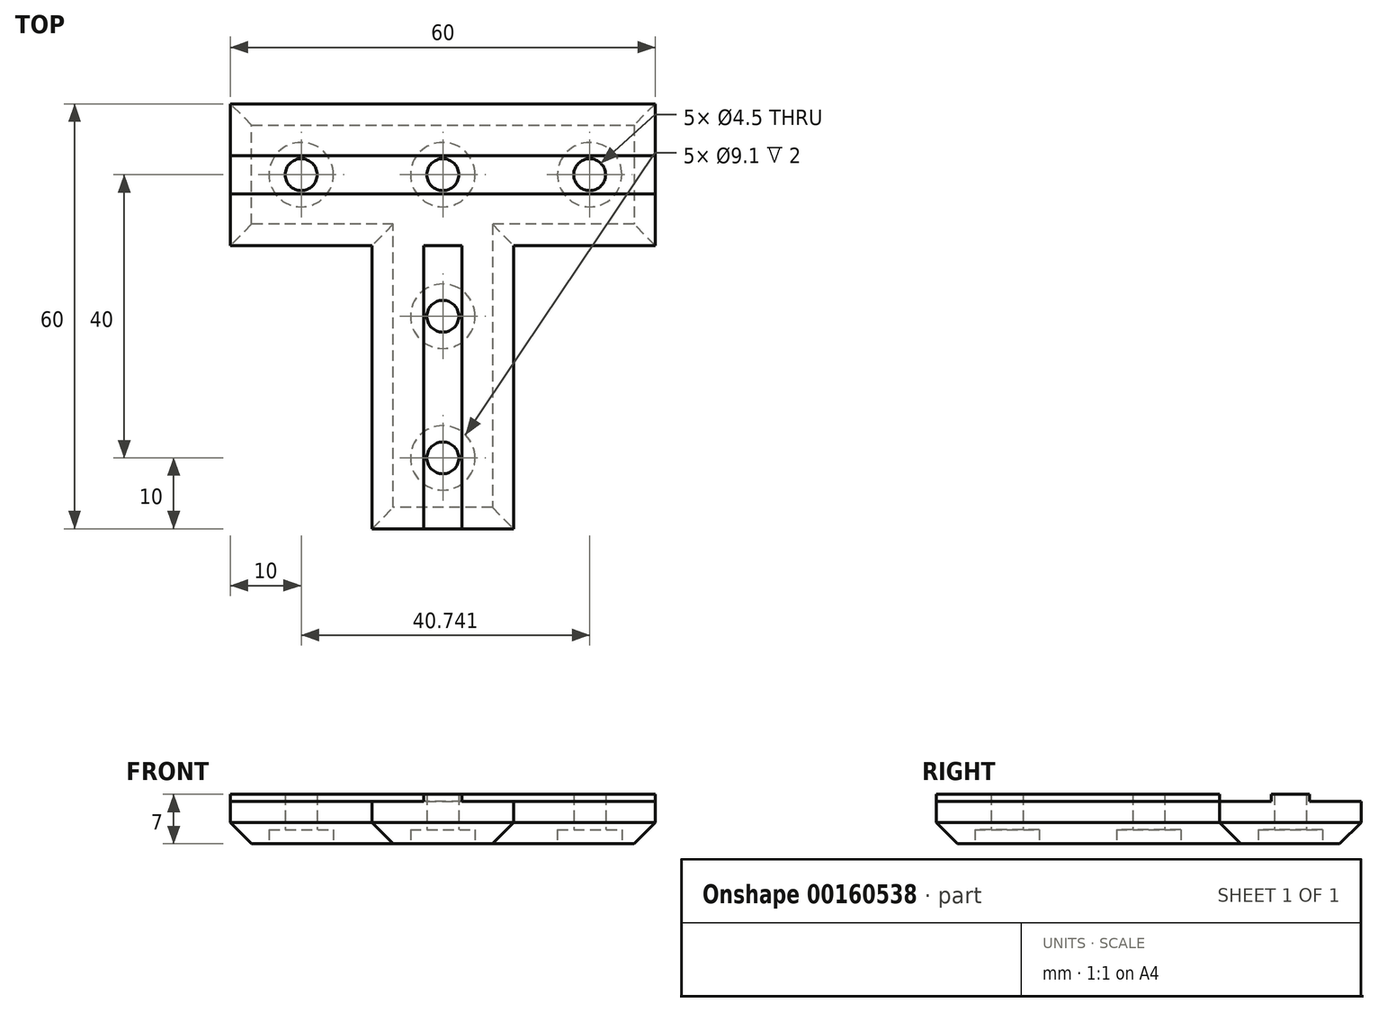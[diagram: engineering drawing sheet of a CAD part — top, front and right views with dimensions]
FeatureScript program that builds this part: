
annotation { "Feature Type Name" : "Feature", "Feature Type Description" : "" }
export const myFeature = defineFeature(function(context is Context, id is Id, definition is map)
    precondition{}
    {
        {
            var Q0;
            Q0=qCreatedBy(makeId("Top.planeOp"),FACE);
            var sketch = newSketch(context, id + "F0", { "sketchPlane" : qUnion([Q0])});
            skLineSegment(sketch, "E0", {"start": v(0, 0) * mm, "end": v(0, 20) * mm, "construction": true});
            skLineSegment(sketch, "E1", {"start": v(0, 0) * mm, "end": v(0, -40) * mm, "construction": true});
            skLineSegment(sketch, "E2", {"start": v(-10, 0) * mm, "end": v(-30, 0) * mm});
            skLineSegment(sketch, "E3", {"start": v(0, 20) * mm, "end": v(-30, 20) * mm});
            skLineSegment(sketch, "E4", {"start": v(-30, 20) * mm, "end": v(-30, 0) * mm});
            skLineSegment(sketch, "E5", {"start": v(0, 20) * mm, "end": v(30, 20) * mm});
            skLineSegment(sketch, "E6", {"start": v(30, 20) * mm, "end": v(30, 0) * mm});
            skLineSegment(sketch, "E7", {"start": v(30, 0) * mm, "end": v(10, 0) * mm});
            skLineSegment(sketch, "E8", {"start": v(0, -40) * mm, "end": v(10, -40) * mm});
            skLineSegment(sketch, "E9", {"start": v(10, -40) * mm, "end": v(10, 0) * mm});
            skLineSegment(sketch, "E10", {"start": v(0, -40) * mm, "end": v(-10, -40) * mm});
            skLineSegment(sketch, "E11", {"start": v(-10, -40) * mm, "end": v(-10, 0) * mm});
            skSolve(sketch);
        }
        {
            var Q0;
            Q0=qSketchRegion(id+"F0",true);
            extrude(context, id + "F1", {"entities" : qUnion([Q0]), "depth" : 6 * mm});
        }
        {
            var Q0;
            Q0=makeQuery(id+"F1.opExtrude","CAP_FACE",FACE,{"disambiguationData":[OSD([sQuery(id+"F0.wireOp",EDGE,"E2"),sQuery(id+"F0.wireOp",EDGE,"E3"),sQuery(id+"F0.wireOp",EDGE,"E4"),sQuery(id+"F0.wireOp",EDGE,"E5"),sQuery(id+"F0.wireOp",EDGE,"E6"),sQuery(id+"F0.wireOp",EDGE,"E7"),sQuery(id+"F0.wireOp",EDGE,"E8"),sQuery(id+"F0.wireOp",EDGE,"E9"),sQuery(id+"F0.wireOp",EDGE,"E10"),sQuery(id+"F0.wireOp",EDGE,"E11")])],"isStart":false});
            var sketch = newSketch(context, id + "F2", { "sketchPlane" : qUnion([Q0])});
            skLineSegment(sketch, "E12", {"start": v(-30, 10) * mm, "end": v(30, 10) * mm, "construction": true});
            skLineSegment(sketch, "E13", {"start": v(0, -40) * mm, "end": v(0, 0) * mm, "construction": true});
            skLineSegment(sketch, "E14", {"start": v(0, 0) * mm, "end": v(-2.71, 0) * mm});
            skLineSegment(sketch, "E15", {"start": v(-2.71, 0) * mm, "end": v(-2.7, -40) * mm});
            skLineSegment(sketch, "E16", {"start": v(2.71, -40) * mm, "end": v(2.71, 0) * mm});
            skLineSegment(sketch, "E17", {"start": v(2.71, 0) * mm, "end": v(0, 0) * mm});
            skLineSegment(sketch, "E18", {"start": v(-2.7, -40) * mm, "end": v(2.71, -40) * mm});
            skLineSegment(sketch, "E19", {"start": v(30, 12.71) * mm, "end": v(30, 7.3) * mm});
            skLineSegment(sketch, "E20", {"start": v(-30, 10) * mm, "end": v(-30, 12.71) * mm});
            skLineSegment(sketch, "E21", {"start": v(-30, 12.71) * mm, "end": v(30, 12.71) * mm});
            skLineSegment(sketch, "E22", {"start": v(-30, 10) * mm, "end": v(-30, 7.3) * mm});
            skLineSegment(sketch, "E23", {"start": v(-30, 7.3) * mm, "end": v(30, 7.3) * mm});
            skSolve(sketch);
        }
        {
            var Q0;
            Q0=qSketchRegion(id+"F2",true);
            extrude(context, id + "F3", {"entities" : qUnion([Q0]), "operationType" : NewBodyOperationType.ADD, "flatOperationType" : FlatOperationType.REMOVE, "offsetDistance" : 25 * mm, "depth" : 1 * mm, "domain" : OperationDomain.MODEL});
        }
        {
            var Q0;
            Q0=makeQuery(id+"F1.opExtrude","CAP_FACE",FACE,{"disambiguationData":[OSD([sQuery(id+"F0.wireOp",EDGE,"E2"),sQuery(id+"F0.wireOp",EDGE,"E3"),sQuery(id+"F0.wireOp",EDGE,"E4"),sQuery(id+"F0.wireOp",EDGE,"E5"),sQuery(id+"F0.wireOp",EDGE,"E6"),sQuery(id+"F0.wireOp",EDGE,"E7"),sQuery(id+"F0.wireOp",EDGE,"E8"),sQuery(id+"F0.wireOp",EDGE,"E9"),sQuery(id+"F0.wireOp",EDGE,"E10"),sQuery(id+"F0.wireOp",EDGE,"E11")])],"isStart":true});
            var sketch = newSketch(context, id + "F4", { "sketchPlane" : qUnion([Q0])});
            skCircle(sketch, "E24", {"center": v(-20, -10) * mm, "radius": 2.25 * mm});
            skCircle(sketch, "E25", {"center": v(0, 10) * mm, "radius": 2.25 * mm});
            skCircle(sketch, "E26", {"center": v(0, 30) * mm, "radius": 2.25 * mm});
            skCircle(sketch, "E27", {"center": v(20.74, -10) * mm, "radius": 2.25 * mm});
            skCircle(sketch, "E28", {"center": v(0, -10) * mm, "radius": 2.25 * mm});
            skSolve(sketch);
        }
        {
            var Q0;
            Q0=qSketchRegion(id+"F4",true);
            extrude(context, id + "F5", {"entities" : qUnion([Q0]), "operationType" : NewBodyOperationType.REMOVE, "endBound" : BoundingType.THROUGH_ALL, "oppositeDirection" : true, "depth" : 25 * mm});
        }
        {
            var Q0;
            Q0=makeQuery(id+"F1.opExtrude","CAP_FACE",FACE,{"disambiguationData":[OSD([sQuery(id+"F0.wireOp",EDGE,"E2"),sQuery(id+"F0.wireOp",EDGE,"E3"),sQuery(id+"F0.wireOp",EDGE,"E4"),sQuery(id+"F0.wireOp",EDGE,"E5"),sQuery(id+"F0.wireOp",EDGE,"E6"),sQuery(id+"F0.wireOp",EDGE,"E7"),sQuery(id+"F0.wireOp",EDGE,"E8"),sQuery(id+"F0.wireOp",EDGE,"E9"),sQuery(id+"F0.wireOp",EDGE,"E10"),sQuery(id+"F0.wireOp",EDGE,"E11")])],"isStart":true});
            var sketch = newSketch(context, id + "F6", { "sketchPlane" : qUnion([Q0])});
            skCircle(sketch, "E29", {"center": v(0, 30) * mm, "radius": 4.55 * mm});
            skCircle(sketch, "E30", {"center": v(0, 10) * mm, "radius": 4.55 * mm});
            skCircle(sketch, "E31", {"center": v(20.74, -10) * mm, "radius": 4.55 * mm});
            skCircle(sketch, "E32", {"center": v(-20, -10) * mm, "radius": 4.55 * mm});
            skCircle(sketch, "E33", {"center": v(0, -10) * mm, "radius": 4.55 * mm});
            skSolve(sketch);
        }
        {
            var Q0;
            Q0=qSketchRegion(id+"F6",true);
            extrude(context, id + "F7", {"entities" : qUnion([Q0]), "operationType" : NewBodyOperationType.REMOVE, "oppositeDirection" : true, "depth" : 2 * mm});
        }
        {
            var Q0;
            Q0=makeQuery(id+"F1.opExtrude","CAP_EDGE",EDGE,{"disambiguationData":[OSD([sQuery(id+"F0.wireOp",EDGE,"E11")])],"isStart":true});
            var Q1;
            Q1=makeQuery(id+"F1.opExtrude","CAP_EDGE",EDGE,{"disambiguationData":[OSD([sQuery(id+"F0.wireOp",EDGE,"E2")])],"isStart":true});
            var Q2;
            Q2=makeQuery(id+"F1.opExtrude","CAP_EDGE",EDGE,{"disambiguationData":[OSD([sQuery(id+"F0.wireOp",EDGE,"E9")])],"isStart":true});
            var Q3;
            Q3=makeQuery(id+"F1.opExtrude","CAP_EDGE",EDGE,{"disambiguationData":[OSD([sQuery(id+"F0.wireOp",EDGE,"E7")])],"isStart":true});
            var Q4;
            Q4=makeQuery(id+"F1.opExtrude","CAP_EDGE",EDGE,{"disambiguationData":[OSD([sQuery(id+"F0.wireOp",EDGE,"E3"),sQuery(id+"F0.wireOp",EDGE,"E5")])],"isStart":true});
            var Q5;
            Q5=makeQuery(id+"F1.opExtrude","CAP_EDGE",EDGE,{"disambiguationData":[OSD([sQuery(id+"F0.wireOp",EDGE,"E6")])],"isStart":true});
            var Q6;
            Q6=makeQuery(id+"F1.opExtrude","CAP_EDGE",EDGE,{"disambiguationData":[OSD([sQuery(id+"F0.wireOp",EDGE,"E4")])],"isStart":true});
            var Q7;
            Q7=makeQuery(id+"F1.opExtrude","CAP_EDGE",EDGE,{"disambiguationData":[OSD([sQuery(id+"F0.wireOp",EDGE,"E8"),sQuery(id+"F0.wireOp",EDGE,"E10")])],"isStart":true});
            chamfer(context, id + "F8", {"entities" : qUnion([Q0, Q1, Q2, Q3, Q4, Q5, Q6, Q7]), "width" : 3 * mm, "tangentPropagation" : true});
        }
    });
